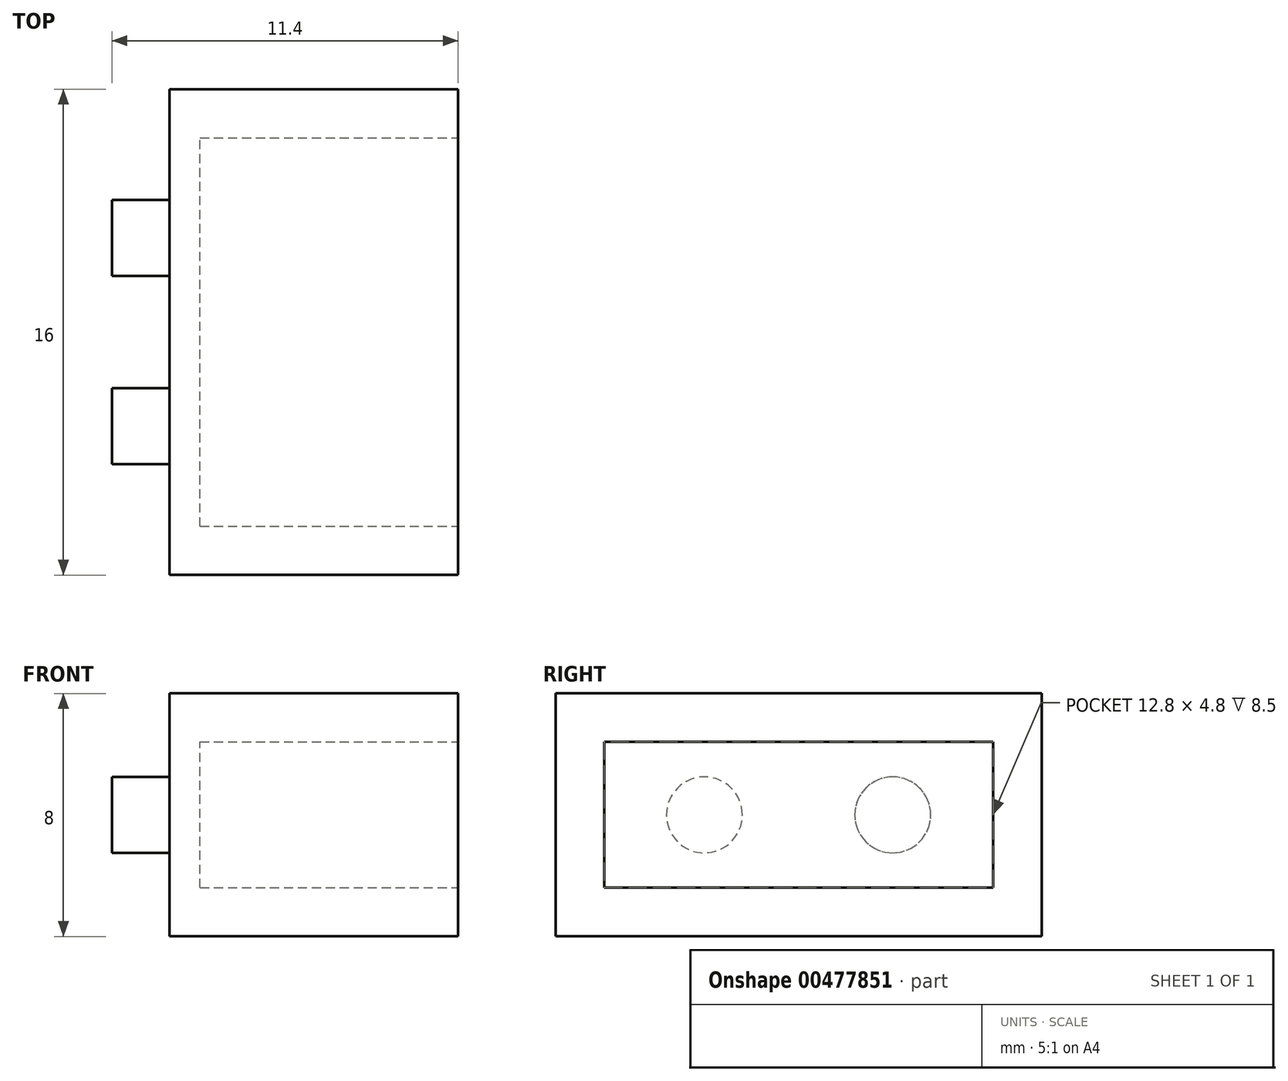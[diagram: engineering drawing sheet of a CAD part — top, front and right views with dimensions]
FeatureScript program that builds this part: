
annotation { "Feature Type Name" : "Feature", "Feature Type Description" : "" }
export const myFeature = defineFeature(function(context is Context, id is Id, definition is map)
    precondition{}
    {
        {
            var Q0;
            Q0=qCreatedBy(makeId("Right.planeOp"),FACE);
            var sketch = newSketch(context, id + "F0", { "sketchPlane" : qUnion([Q0])});
            skLineSegment(sketch, "E0.bottom", {"start": v(49.78, 25.94) * mm, "end": v(33.78, 25.94) * mm});
            skLineSegment(sketch, "E0.top", {"start": v(49.78, 17.94) * mm, "end": v(33.78, 17.94) * mm});
            skLineSegment(sketch, "E0.left", {"start": v(49.78, 25.94) * mm, "end": v(49.78, 17.94) * mm});
            skLineSegment(sketch, "E0.right", {"start": v(33.78, 25.94) * mm, "end": v(33.78, 17.94) * mm});
            skSolve(sketch);
        }
        {
            var Q0;
            Q0=makeQuery(id+"F0.imprint","IMPRINT",FACE,{"disambiguationData":[TD([[makeQuery(id+"F0.imprint","IMPRINT",EDGE,{"derivedFrom":sQuery(id+"F0.wireOp",EDGE,"E0.bottom")}),1.0]])]});
            extrude(context, id + "F1", {"entities" : qUnion([Q0]), "depth" : 9.5 * mm});
        }
        {
            var Q0;
            Q0=makeQuery(id+"F1.opExtrude","CAP_FACE",FACE,{"disambiguationData":[OSD([sQuery(id+"F0.wireOp",EDGE,"E0.bottom"),sQuery(id+"F0.wireOp",EDGE,"E0.top"),sQuery(id+"F0.wireOp",EDGE,"E0.left"),sQuery(id+"F0.wireOp",EDGE,"E0.right")])],"isStart":true});
            var sketch = newSketch(context, id + "F2", { "sketchPlane" : qUnion([Q0])});
            skCircle(sketch, "E1", {"center": v(-38.68, 21.94) * mm, "radius": 1.25 * mm});
            skCircle(sketch, "E2", {"center": v(-44.88, 21.94) * mm, "radius": 1.25 * mm});
            skSolve(sketch);
        }
        {
            var Q0;
            Q0=makeQuery(id+"F2.imprint","IMPRINT",FACE,{"disambiguationData":[TD([[makeQuery(id+"F2.imprint","IMPRINT",EDGE,{"derivedFrom":sQuery(id+"F2.wireOp",EDGE,"E2")}),1.0]])]});
            var Q1;
            Q1=makeQuery(id+"F2.imprint","IMPRINT",FACE,{"disambiguationData":[TD([[makeQuery(id+"F2.imprint","IMPRINT",EDGE,{"derivedFrom":sQuery(id+"F2.wireOp",EDGE,"E1")}),1.0]])]});
            var Q2;
            Q2 = qSketchRegion(id + "F4", true);
            extrude(context, id + "F3", {"entities" : qUnion([Q0, Q1, Q2]), "operationType" : NewBodyOperationType.ADD, "depth" : 1.9 * mm});
        }
        {
            var Q0;
            Q0=makeQuery(id+"F1.opExtrude","CAP_FACE",FACE,{"disambiguationData":[OSD([sQuery(id+"F0.wireOp",EDGE,"E0.bottom"),sQuery(id+"F0.wireOp",EDGE,"E0.top"),sQuery(id+"F0.wireOp",EDGE,"E0.left"),sQuery(id+"F0.wireOp",EDGE,"E0.right")])],"isStart":false});
            var sketch = newSketch(context, id + "F4", { "sketchPlane" : qUnion([Q0])});
            skLineSegment(sketch, "E3", {"start": v(48.18, 19.54) * mm, "end": v(48.18, 24.34) * mm});
            skLineSegment(sketch, "E4", {"start": v(48.18, 24.34) * mm, "end": v(35.38, 24.34) * mm});
            skLineSegment(sketch, "E5", {"start": v(35.38, 24.34) * mm, "end": v(35.38, 19.54) * mm});
            skLineSegment(sketch, "E6", {"start": v(35.38, 19.54) * mm, "end": v(48.18, 19.54) * mm});
            skSolve(sketch);
        }
        {
            var Q0;
            Q0=qCreatedBy(makeId("Right.planeOp"),FACE);
            var sketch = newSketch(context, id + "F5", { "sketchPlane" : qUnion([Q0])});
            skSolve(sketch);
        }
        {
            var Q0;
            Q0 = qSketchRegion(id + "F5", true);
            var Q1;
            Q1=makeQuery(id+"F4.imprint","IMPRINT",FACE,{"disambiguationData":[TD([[makeQuery(id+"F4.imprint","IMPRINT",EDGE,{"derivedFrom":sQuery(id+"F4.wireOp",EDGE,"E3")}),1.0]])]});
            extrude(context, id + "F6", {"entities" : qUnion([Q0, Q1]), "operationType" : NewBodyOperationType.REMOVE, "oppositeDirection" : true, "depth" : 8.5 * mm});
        }
    });
